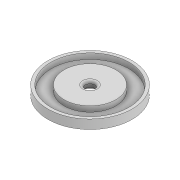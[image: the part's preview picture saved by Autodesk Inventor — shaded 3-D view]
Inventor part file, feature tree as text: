
AUTODESK INVENTOR PART (.ipt)
format: ipt  version: 2021.3 (Build 253353000, 353)  size: 117,248 bytes
history: native  units: mm
features: extrude x2, sketch x1, draft x1, hole x1, chamfer x1, fillet x1
ambient origin geometry x8: Origin, YZ Plane, XZ Plane, XY Plane, X Axis, Y Axis, Z Axis, Center Point
bodies: Solid1 (feature_tree)
feature tree (7):
  sketch  "Sketch1"  dims[d0=42.7mm d1=28.5mm d3=1.8mm d4=5.0mm d5=0.0mm d6=2.0mm d7=0.0mm d8=0.575959mm d9=5.3mm d10=6.0mm d11=10.0mm d12=12.0mm d13=90.0deg d14=8.0mm d15=20.594885mm d16=2.0mm d17=2.0mm d18=45.0deg d19=1.4mm]
  extrude  "Extrusion1"  Depth=1.4mm
  extrude  "Extrusion2"  Depth=1.4mm
  draft  "FaceDraft1"
  hole  "Hole1"  [1 undecoded]
  chamfer  "Chamfer1"  Distance=2.0mm
  fillet  "Fillet1"  Radius=0.575959mm
note: 1 required parameter value undecoded (feature->parameter linkage not recoverable at this tier; creation-order binding heuristic only, values carry confidence <= 0.55)
